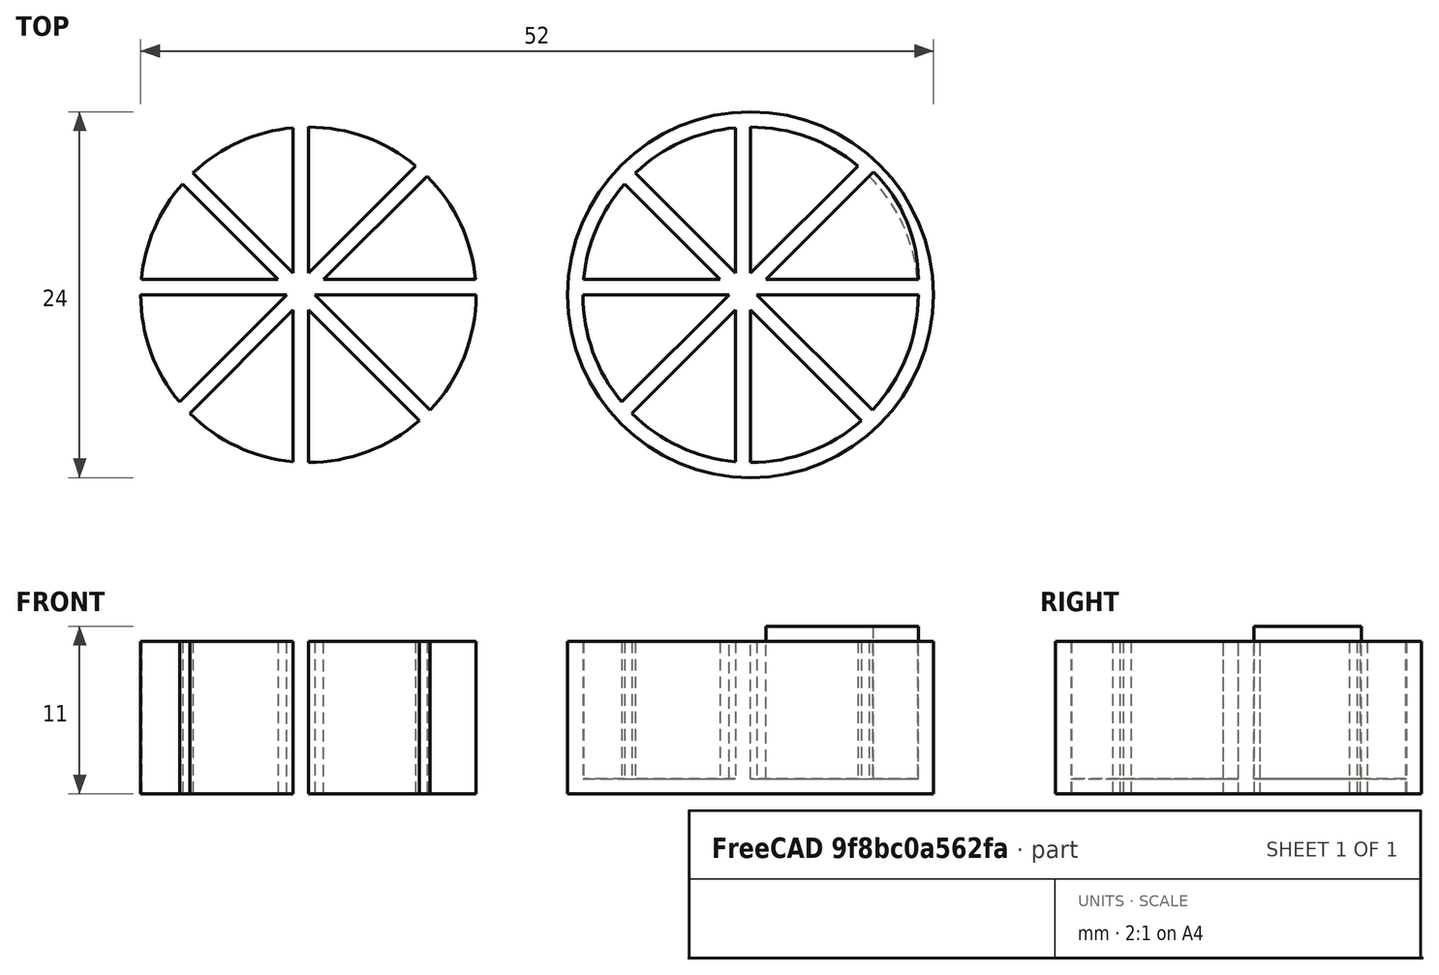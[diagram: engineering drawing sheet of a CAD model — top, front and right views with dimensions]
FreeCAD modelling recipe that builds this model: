
FCSTD DOCUMENT  (FreeCAD 1.0R39319 (Git))
Label: ojt1_t11r02_trivial
License: All rights reserved
LicenseURL: https://en.wikipedia.org/wiki/All_rights_reserved
objects: Part::Cut×9, Part::Box×8, Part::Cylinder×4
note: 21 computed .brp shape members not serialized (recipe doc carries the construction recipe); baked Part::Feature solids carry a one-line shape summary decoded from their .brp

FEATURE [Part::Cylinder] Cylinder  label="Cilindre"
  Angle = 360
  AttacherType = Attacher::AttachEngine3D
  FirstAngle = 0
  Height = 10
  Radius = 12
  SecondAngle = 0
FEATURE [Part::Cylinder] Cylinder001  label="Cilindre001"
  Angle = 360
  AttacherType = Attacher::AttachEngine3D
  FirstAngle = 0
  Height = 10
  Radius = 11
  SecondAngle = 0
FEATURE [Part::Box] Box  label="Cub"
  AttacherType = Attacher::AttachEngine3D
  Height = 10
  Length = 30
  Placement = pos=(-14,0,0) rot=(0,0,1;0rad)
  Width = 1
FEATURE [Part::Box] Box001  label="Cub001"
  AttacherType = Attacher::AttachEngine3D
  Height = 10
  Length = 30
  Placement = pos=(0,-15,0) rot=(0,0,1;1.5708rad)
  Width = 1
FEATURE [Part::Box] Box002  label="Cub002"
  AttacherType = Attacher::AttachEngine3D
  Height = 10
  Length = 45
  Placement = pos=(-15,-15,0) rot=(0,0,1;0.785398rad)
  Width = 1
FEATURE [Part::Box] Box003  label="Cub003"
  AttacherType = Attacher::AttachEngine3D
  Height = 10
  Length = 40
  Placement = pos=(-18,17,0) rot=(0,0,-1;0.785398rad)
  Width = 1
FEATURE [Part::Cut] Cut
  Base = -> Cylinder001
  Refine = true
  Tool = -> Box
FEATURE [Part::Cut] Cut001
  Base = -> Cut
  Refine = true
  Tool = -> Box003
FEATURE [Part::Cut] Cut002
  Base = -> Cut001
  Refine = true
  Tool = -> Box002
FEATURE [Part::Cut] Cut003
  Base = -> Cut002
  Placement = pos=(0,0,1) rot=(0,0,1;0rad)
  Refine = true
  Tool = -> Box001
FEATURE [Part::Box] Box004  label="Cub004"
  AttacherType = Attacher::AttachEngine3D
  Height = 10
  Length = 30
  Placement = pos=(-14,0,0) rot=(0,0,1;0rad)
  Width = 1
FEATURE [Part::Box] Box005  label="Cub005"
  AttacherType = Attacher::AttachEngine3D
  Height = 10
  Length = 30
  Placement = pos=(0,-15,0) rot=(0,0,1;1.5708rad)
  Width = 1
FEATURE [Part::Box] Box006  label="Cub006"
  AttacherType = Attacher::AttachEngine3D
  Height = 10
  Length = 45
  Placement = pos=(-15,-15,0) rot=(0,0,1;0.785398rad)
  Width = 1
FEATURE [Part::Box] Box007  label="Cub007"
  AttacherType = Attacher::AttachEngine3D
  Height = 10
  Length = 40
  Placement = pos=(-18,17,0) rot=(0,0,-1;0.785398rad)
  Width = 1
FEATURE [Part::Cylinder] Cylinder002  label="Cilindre002"
  Angle = 360
  AttacherType = Attacher::AttachEngine3D
  FirstAngle = 0
  Height = 10
  Radius = 11
  SecondAngle = 0
FEATURE [Part::Cut] Cut004
  Base = -> Cylinder002
  Refine = true
  Tool = -> Box004
FEATURE [Part::Cut] Cut005
  Base = -> Cut004
  Refine = true
  Tool = -> Box007
FEATURE [Part::Cut] Cut006
  Base = -> Cut005
  Refine = true
  Tool = -> Box006
FEATURE [Part::Cut] Cut007
  Base = -> Cut006
  Placement = pos=(-29,0,0) rot=(0,0,1;0rad)
  Refine = true
  Tool = -> Box005
FEATURE [Part::Cut] Cut008
  Base = -> Cylinder
  Refine = true
  Tool = -> Cut003
FEATURE [Part::Cylinder] Cylinder003  label="Cilindre003"
  Angle = 45
  AttacherType = Attacher::AttachEngine3D
  FirstAngle = 0
  Height = 10
  Placement = pos=(1,1,1) rot=(0,0,1;0rad)
  Radius = 10
  SecondAngle = 0
